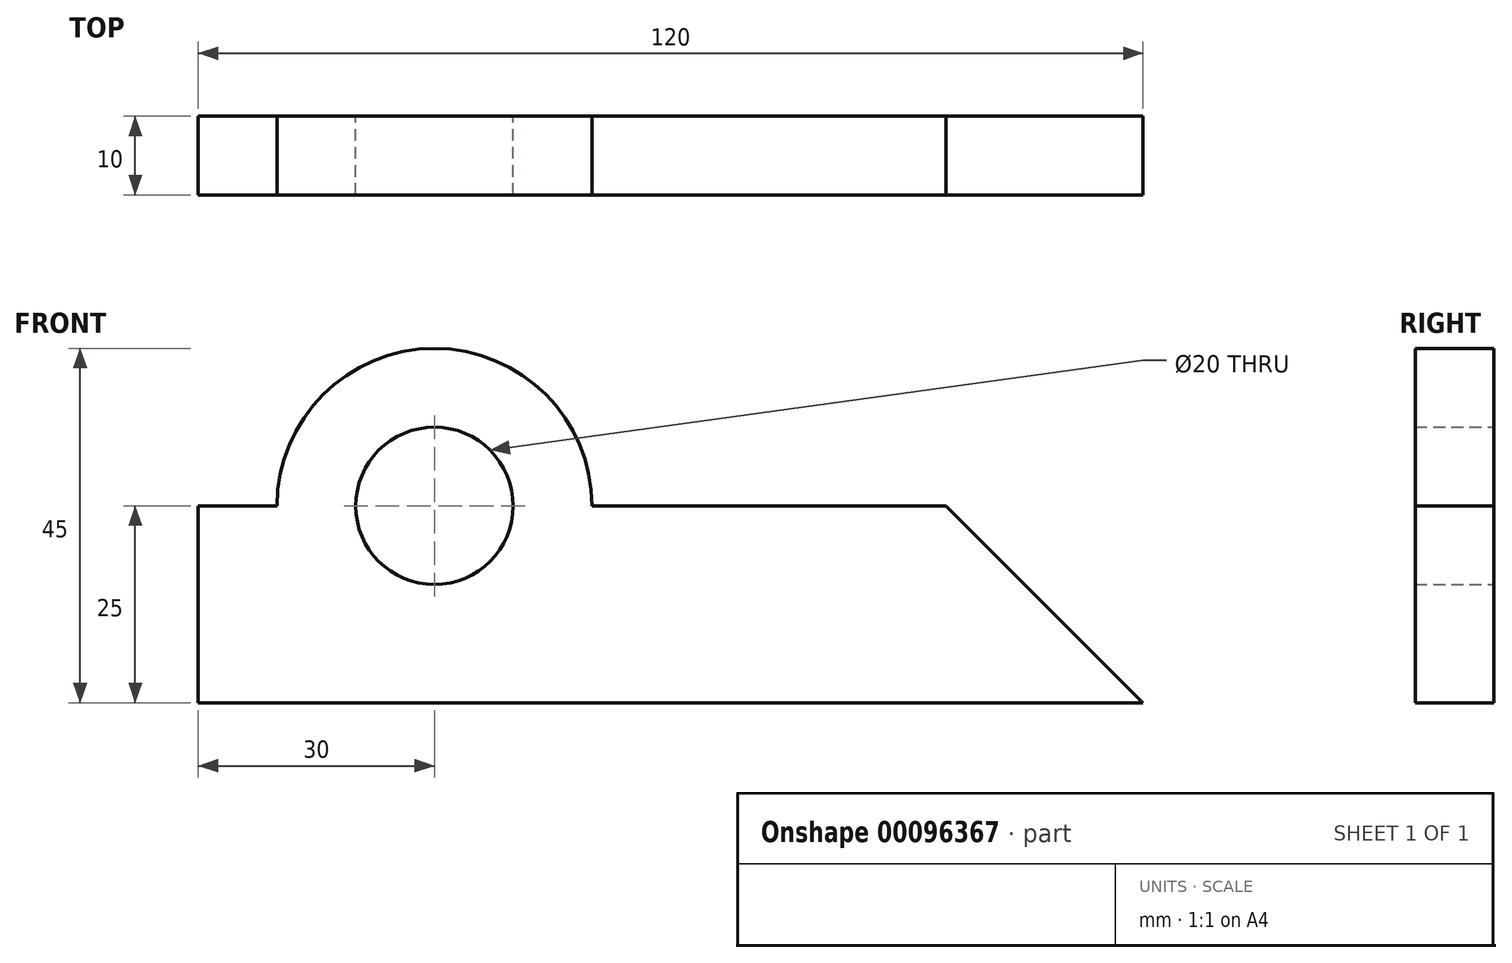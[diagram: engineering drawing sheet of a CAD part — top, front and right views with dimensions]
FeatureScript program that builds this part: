
annotation { "Feature Type Name" : "Feature", "Feature Type Description" : "" }
export const myFeature = defineFeature(function(context is Context, id is Id, definition is map)
    precondition{}
    {
        {
            var Q0;
            Q0=qCreatedBy(makeId("Front.planeOp"),FACE);
            var sketch = newSketch(context, id + "F0", { "sketchPlane" : qUnion([Q0])});
            skLineSegment(sketch, "E0", {"start": v(0, 0) * mm, "end": v(120, 0) * mm});
            skLineSegment(sketch, "E1", {"start": v(120, 0) * mm, "end": v(95, 25) * mm});
            skLineSegment(sketch, "E2", {"start": v(95, 25) * mm, "end": v(50, 25) * mm});
            skLineSegment(sketch, "E3", {"start": v(0, 25) * mm, "end": v(0, 0) * mm});
            skLineSegment(sketch, "E4", {"start": v(10, 25) * mm, "end": v(0, 25) * mm});
            skCircle(sketch, "E5", {"center": v(30, 25) * mm, "radius": 10 * mm});
            skArc(sketch, "E6", {"start": v(50, 25) * mm, "mid": v(30, 45) * mm, "end": v(10, 25) * mm});
            skSolve(sketch);
        }
        {
            var Q0;
            Q0=makeQuery(id+"F0.imprint","IMPRINT",FACE,{"disambiguationData":[TD([[makeQuery(id+"F0.imprint","IMPRINT",EDGE,{"derivedFrom":sQuery(id+"F0.wireOp",EDGE,"E0")}),1.0]])]});
            extrude(context, id + "F1", {"entities" : qUnion([Q0]), "depth" : 10 * mm});
        }
    });
